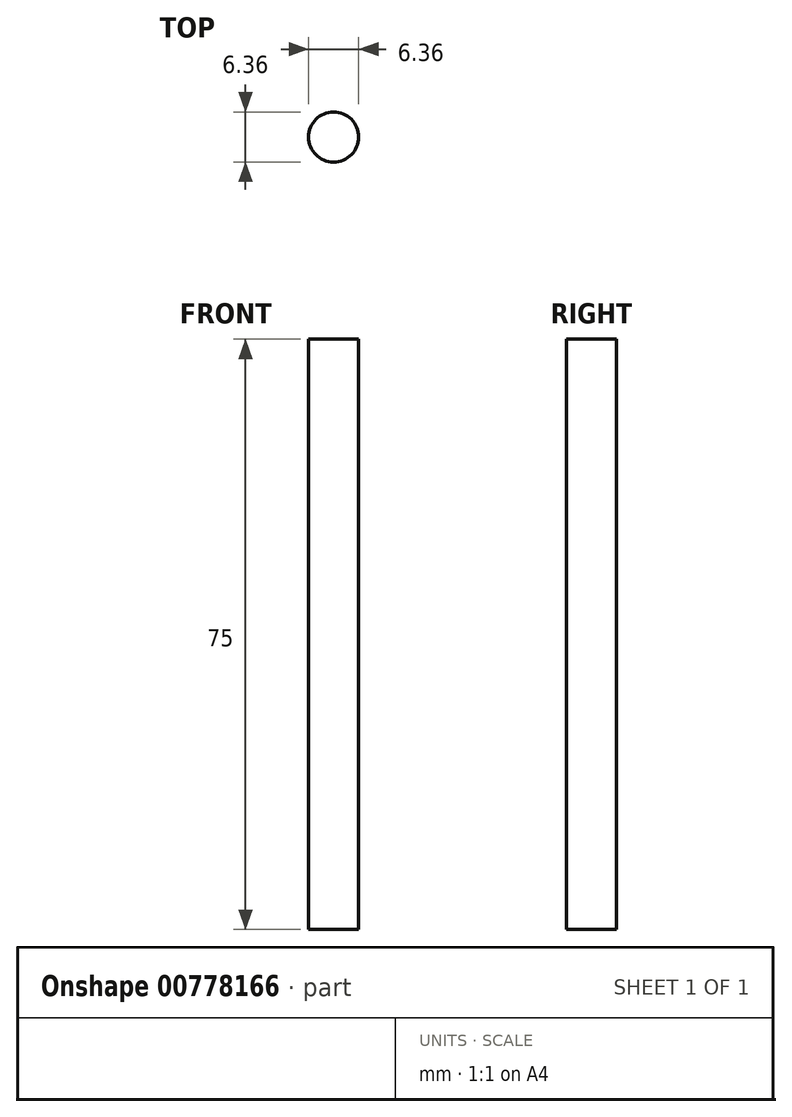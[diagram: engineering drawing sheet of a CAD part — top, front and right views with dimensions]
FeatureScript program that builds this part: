
annotation { "Feature Type Name" : "Feature", "Feature Type Description" : "" }
export const myFeature = defineFeature(function(context is Context, id is Id, definition is map)
    precondition{}
    {
        {
            var Q0;
            Q0=qCreatedBy(makeId("Top.planeOp"),FACE);
            var sketch = newSketch(context, id + "F0", { "sketchPlane" : qUnion([Q0])});
            skCircle(sketch, "E0", {"center": v(0, 0) * mm, "radius": 3.18 * mm});
            skSolve(sketch);
        }
        {
            var Q0;
            Q0=makeQuery(id+"F0.imprint","IMPRINT",FACE,{"disambiguationData":[TD([[makeQuery(id+"F0.imprint","IMPRINT",EDGE,{"derivedFrom":sQuery(id+"F0.wireOp",EDGE,"E0")}),1.0]])]});
            extrude(context, id + "F1", {"entities" : qUnion([Q0]), "depth" : 75 * mm, "offsetDistance" : 25 * mm});
        }
    });
